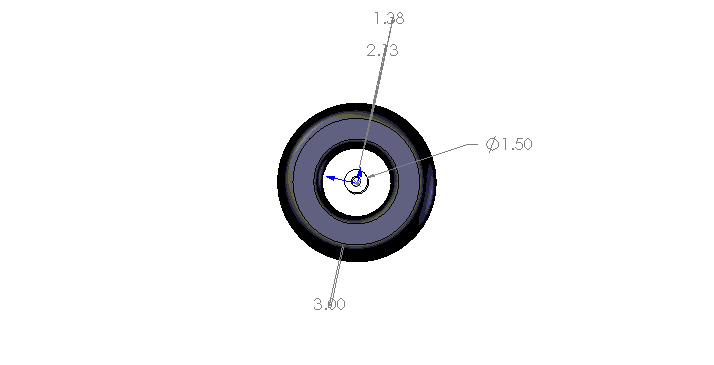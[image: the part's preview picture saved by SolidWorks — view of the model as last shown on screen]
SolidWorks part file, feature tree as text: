
SOLIDWORKS PART (.sldprt)
format: sldprt  version: not decoded by parser v0  size: 208,384 bytes
history: native  units: mm
features: sketch x5, cut_extrude x3, extrude x2, fillet x2 + 1 further entry (+10 scaffold rows collapsed)
feature tree (23):
  "Annotations"  RD1=53.975mm RD2=76.2mm RD3=34.925mm RD4=38.1mm
  scaffold x10  (default folders/planes/origin — collapsed)
  sketch  "Sketch1"  dims[D1=254.0mm]
  extrude  "Extrude1"  Depth=76.2mm
  sketch  "Sketch3"  dims[D1=107.95mm]
  cut_extrude  "Cut-Extrude1"  Depth=34.925mm
  sketch  "Sketch4"  dims[D1=111.125mm]
  cut_extrude  "Cut-Extrude2"  Depth=34.925mm
  sketch  "Sketch2"  dims[D1=38.1mm]
  extrude  "Extrude2"  Depth=12.7mm
  sketch  "Sketch5"  dims[D1=15.875mm]
  cut_extrude  "Cut-Extrude3"  [1 undecoded]
  fillet  "Fillet1"  Radius=25.4mm
  fillet  "Fillet2"  Radius=12.7mm
decode coverage: 11 of 12 modeling features carry decoded parameters; 1 rows unclassified (native names shown)
note: 1 parameter value undecoded
note: suppression state not decoded; provenance and decode notes live in map.json
